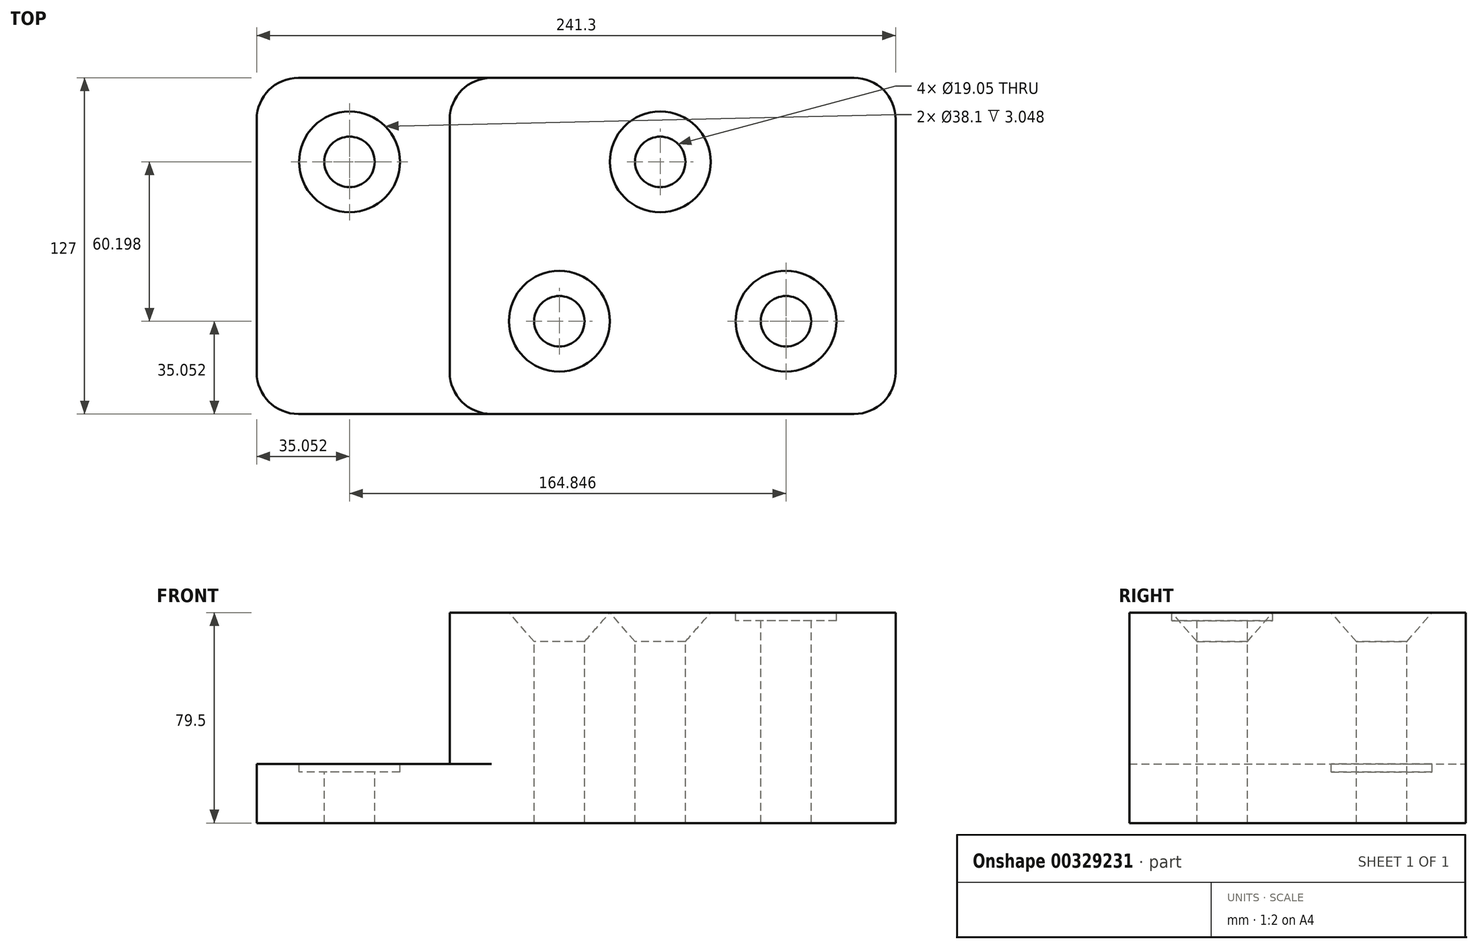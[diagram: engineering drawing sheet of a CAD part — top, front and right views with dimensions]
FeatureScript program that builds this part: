
annotation { "Feature Type Name" : "Feature", "Feature Type Description" : "" }
export const myFeature = defineFeature(function(context is Context, id is Id, definition is map)
    precondition{}
    {
        {
            var Q0;
            Q0=qCreatedBy(makeId("Front.planeOp"),FACE);
            var sketch = newSketch(context, id + "F0", { "sketchPlane" : qUnion([Q0])});
            skLineSegment(sketch, "E0", {"start": v(0, 0) * mm, "end": v(241.3, 0) * mm});
            skLineSegment(sketch, "E1", {"start": v(241.3, 0) * mm, "end": v(241.3, 79.5) * mm});
            skLineSegment(sketch, "E2", {"start": v(241.3, 79.5) * mm, "end": v(72.9, 79.5) * mm});
            skLineSegment(sketch, "E3", {"start": v(72.9, 79.5) * mm, "end": v(72.9, 22.35) * mm});
            skLineSegment(sketch, "E4", {"start": v(72.9, 22.35) * mm, "end": v(0, 22.35) * mm});
            skLineSegment(sketch, "E5", {"start": v(0, 22.35) * mm, "end": v(0, 0) * mm});
            skSolve(sketch);
        }
        {
            var Q0;
            Q0=makeQuery(id+"F0.imprint","IMPRINT",FACE,{"disambiguationData":[TD([[makeQuery(id+"F0.imprint","IMPRINT",EDGE,{"derivedFrom":sQuery(id+"F0.wireOp",EDGE,"E0")}),1.0]])]});
            extrude(context, id + "F1", {"entities" : qUnion([Q0]), "depth" : 127 * mm});
        }
        {
            var Q0;
            Q0=makeQuery(id+"F1.opExtrude","SWEPT_FACE",FACE,{"disambiguationData":[OSD([sQuery(id+"F0.wireOp",EDGE,"E2")])]});
            var sketch = newSketch(context, id + "F2", { "sketchPlane" : qUnion([Q0])});
            skPoint(sketch, "E6", {"position": v(199.9, -91.95) * mm});
            skPoint(sketch, "E7", {"position": v(114.3, -91.95) * mm});
            skPoint(sketch, "E8", {"position": v(152.4, -31.75) * mm});
            skSolve(sketch);
        }
        {
            var Q0;
            Q0=makeQuery(id+"F1.opExtrude","SWEPT_FACE",FACE,{"disambiguationData":[OSD([sQuery(id+"F0.wireOp",EDGE,"E4")])]});
            var sketch = newSketch(context, id + "F3", { "sketchPlane" : qUnion([Q0])});
            skPoint(sketch, "E9", {"position": v(35.05, -31.75) * mm});
            skSolve(sketch);
        }
        {
            var Q0;
            Q0=sQuery(id+"F3.wireOp",VERTEX,"E9");
            var Q1;
            Q1=sQuery(id+"F2.wireOp",VERTEX,"E6");
            var Q2;
            Q2=makeQuery(id+"F1.opExtrude","SWEPT_BODY",BODY,{"disambiguationData":[OSD([sQuery(id+"F0.wireOp",EDGE,"E0"),sQuery(id+"F0.wireOp",EDGE,"E1"),sQuery(id+"F0.wireOp",EDGE,"E2"),sQuery(id+"F0.wireOp",EDGE,"E3"),sQuery(id+"F0.wireOp",EDGE,"E4"),sQuery(id+"F0.wireOp",EDGE,"E5")])]});
            hole(context, id + "F4", {"style" : HoleStyle.C_BORE, "endStyle" : HoleEndStyle.THROUGH, "holeDiameter" : 19.05 * mm, "cBoreDiameter" : 38.1 * mm, "cBoreDepth" : 3.05 * mm, "tappedDepth" : 12.7 * mm, "tapClearance" : 3, "locations" : qUnion([Q0, Q1]), "scope" : qUnion([Q2])});
        }
        {
            var Q0;
            Q0=sQuery(id+"F2.wireOp",VERTEX,"E7");
            var Q1;
            Q1=sQuery(id+"F2.wireOp",VERTEX,"E8");
            var Q2;
            Q2=makeQuery(id+"F1.opExtrude","SWEPT_BODY",BODY,{"disambiguationData":[OSD([sQuery(id+"F0.wireOp",EDGE,"E0"),sQuery(id+"F0.wireOp",EDGE,"E1"),sQuery(id+"F0.wireOp",EDGE,"E2"),sQuery(id+"F0.wireOp",EDGE,"E3"),sQuery(id+"F0.wireOp",EDGE,"E4"),sQuery(id+"F0.wireOp",EDGE,"E5")])]});
            hole(context, id + "F5", {"style" : HoleStyle.C_SINK, "endStyle" : HoleEndStyle.THROUGH, "holeDiameter" : 19.05 * mm, "cSinkDiameter" : 38.1 * mm, "cSinkAngle" : 82 * degree, "tappedDepth" : 12.7 * mm, "tapClearance" : 3, "locations" : qUnion([Q0, Q1]), "scope" : qUnion([Q2])});
        }
        {
            var Q0;
            Q0=makeQuery(id+"F1.opExtrude","CAP_EDGE",EDGE,{"disambiguationData":[OSD([sQuery(id+"F0.wireOp",EDGE,"E5")])],"isStart":true});
            var Q1;
            Q1=makeQuery(id+"F1.opExtrude","CAP_EDGE",EDGE,{"disambiguationData":[OSD([sQuery(id+"F0.wireOp",EDGE,"E3")])],"isStart":true});
            var Q2;
            Q2=makeQuery(id+"F1.opExtrude","CAP_EDGE",EDGE,{"disambiguationData":[OSD([sQuery(id+"F0.wireOp",EDGE,"E3")])],"isStart":false});
            var Q3;
            Q3=makeQuery(id+"F1.opExtrude","CAP_EDGE",EDGE,{"disambiguationData":[OSD([sQuery(id+"F0.wireOp",EDGE,"E5")])],"isStart":false});
            var Q4;
            Q4=makeQuery(id+"F1.opExtrude","CAP_EDGE",EDGE,{"disambiguationData":[OSD([sQuery(id+"F0.wireOp",EDGE,"E1")])],"isStart":false});
            var Q5;
            Q5=makeQuery(id+"F1.opExtrude","CAP_EDGE",EDGE,{"disambiguationData":[OSD([sQuery(id+"F0.wireOp",EDGE,"E1")])],"isStart":true});
            fillet(context, id + "F6", {"entities" : qUnion([Q0, Q1, Q2, Q3, Q4, Q5]), "radius" : 15.75 * mm, "tangentPropagation" : true, "allowEdgeOverflow" : false});
        }
    });
